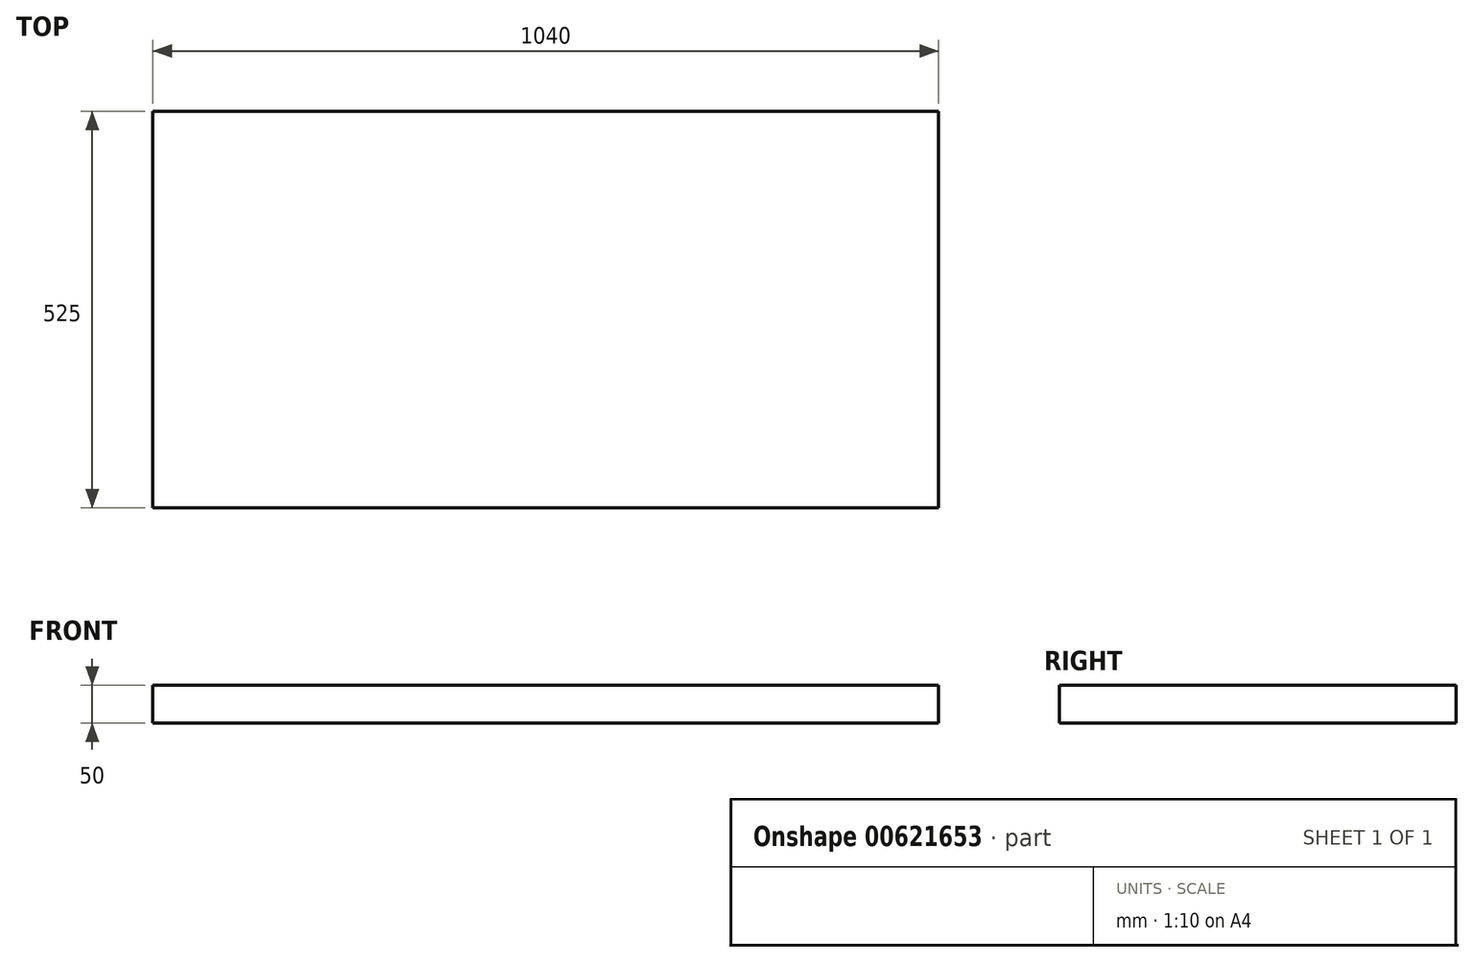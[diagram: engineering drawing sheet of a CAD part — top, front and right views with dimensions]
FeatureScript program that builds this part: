
annotation { "Feature Type Name" : "Feature", "Feature Type Description" : "" }
export const myFeature = defineFeature(function(context is Context, id is Id, definition is map)
    precondition{}
    {
        {
            var Q0;
            Q0=qCreatedBy(makeId("Top.planeOp"),FACE);
            var sketch = newSketch(context, id + "F0", { "sketchPlane" : qUnion([Q0])});
            skLineSegment(sketch, "E0.bottom", {"start": v(0, 0) * mm, "end": v(1040, 0) * mm});
            skLineSegment(sketch, "E0.top", {"start": v(0, 525) * mm, "end": v(1040, 525) * mm});
            skLineSegment(sketch, "E0.left", {"start": v(0, 0) * mm, "end": v(0, 525) * mm});
            skLineSegment(sketch, "E0.right", {"start": v(1040, 0) * mm, "end": v(1040, 525) * mm});
            skSolve(sketch);
        }
        {
            var Q0;
            Q0 = qSketchRegion(id + "F0", true);
            extrude(context, id + "F1", {"entities" : qUnion([Q0]), "depth" : 50 * mm, "offsetDistance" : 25 * mm});
        }
    });
